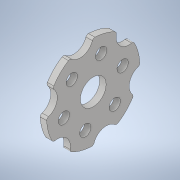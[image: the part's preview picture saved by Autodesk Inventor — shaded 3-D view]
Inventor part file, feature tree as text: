
AUTODESK INVENTOR PART (.ipt)
format: ipt  version: 2021 (Build 250183000, 183)  size: 176,640 bytes
history: native  units: in
note: dims shown in document units (in); Inventor stores cm internally (conversion verified against a paired STEP export)
features: extrude x1, fillet x1, sketch x1
ambient origin geometry x8: Origin, YZ Plane, XZ Plane, XY Plane, X Axis, Y Axis, Z Axis, Center Point
bodies: Solid1 (feature_tree)
feature tree (3):
  extrude  "Extrusion1"  Depth=0.125in
  fillet  "Fillet1"  Radius=0.55in
  sketch  "Sketch1"  dims[d0=4.517in d1=2.952in d2=0.55in d3=45.0deg d4=2.3622in d6=360.0deg d8=1.25in d12=1.25in d16=15.0deg d17=2.3622in d19=360.0deg d21=0.3125in d22=0.0in d23=0.125in d24=0.851in d25=2.3676in]
